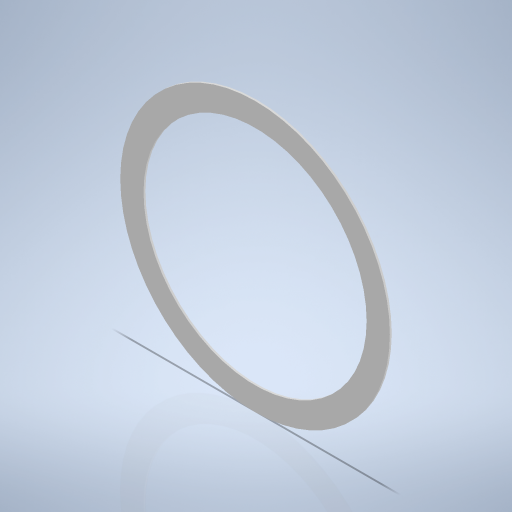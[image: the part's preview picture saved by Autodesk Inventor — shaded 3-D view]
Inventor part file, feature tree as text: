
AUTODESK INVENTOR PART (.ipt)
format: ipt  version: 2024 (Build 280153000, 153)  size: 241,664 bytes
history: native  units: mm
features: extrude x1, sketch x1
ambient origin geometry x8: Origin, YZ Plane, XZ Plane, XY Plane, X Axis, Y Axis, Z Axis, Center Point
bodies: Volumenkörper1 (feature_tree)
feature tree (2):
  extrude  "Extrusion1"  Depth=0.2mm
  sketch  "Skizze1"  dims[d0=29.0mm d1=24.0mm d2=0.2mm d3=0.0mm]
